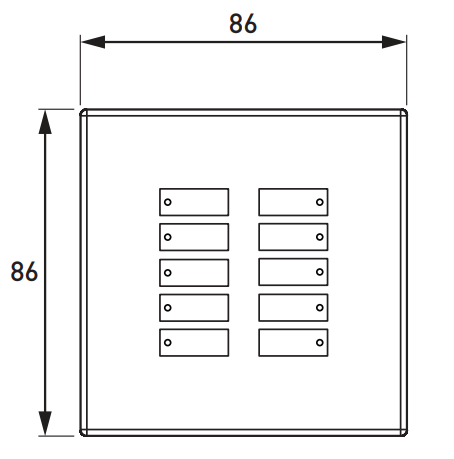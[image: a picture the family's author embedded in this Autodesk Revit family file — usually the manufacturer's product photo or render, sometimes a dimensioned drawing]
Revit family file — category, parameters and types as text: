
# Revit family: Enocean Panel _184X
name_source: partatom
category: Electrical Fixtures
revit_build: Autodesk Revit 2018 (Build: 20170223_1515(x64)
units: mm (PartAtom-declared; Revit-internal decimal feet)

## family parameters
Always vertical = Yes
Cut with Voids When Loaded = No
Maintain Annotation Orientation = No
Part Type = Normal
Room Calculation Point = No
Round Connector Dimension = Use Diameter
Shared = No
Work Plane-Based = Yes

## types (1)
- Dual Rocker Switch_Black/White
    Ambient temperature = 0 °C to +50 °C
    Connections = No wiring (power or communications) is required.
    Default Elevation = 0 mm  [stored 0 ft]
    Dimensions = 86 mm × 86 mm × 15 mm
    Environment = Complies with WEEE and RoHS directives
    Frame = Plastic (183 & 184)
    IP code = IP30
    Manufacturer = Helvar
    Material: = Switch rockers: plastic
    Model = 184 W/184 B
    Mounting = Mount to back box, or mount on glass or flat surface
    Operating frequency = 868 MHz ISM band (Europe)
    Power = Signal power is generated by pressing the EnOcean button
    RED 2014/53/EU = EN 301489-3 EN 300220-2
    Range: = 30 m (unobstructed space)
    Relative humidity = Max. 90 %, noncondensing
    Safety = EN 60950-1
    Storage temperature = –10 °C to +70 °C
    Switch colour = 18xW: white 18xB: black
    Weight = 150 g
    Wireless protocol = ISO/IEC 14543–3–10

note: [stored X ft] marks values corroborated as IEEE doubles in the binary element streams (Revit-internal decimal feet)

## geometry (parser evidence)
native form markers: Sweep x16
no freeform markers — native parametric forms only
